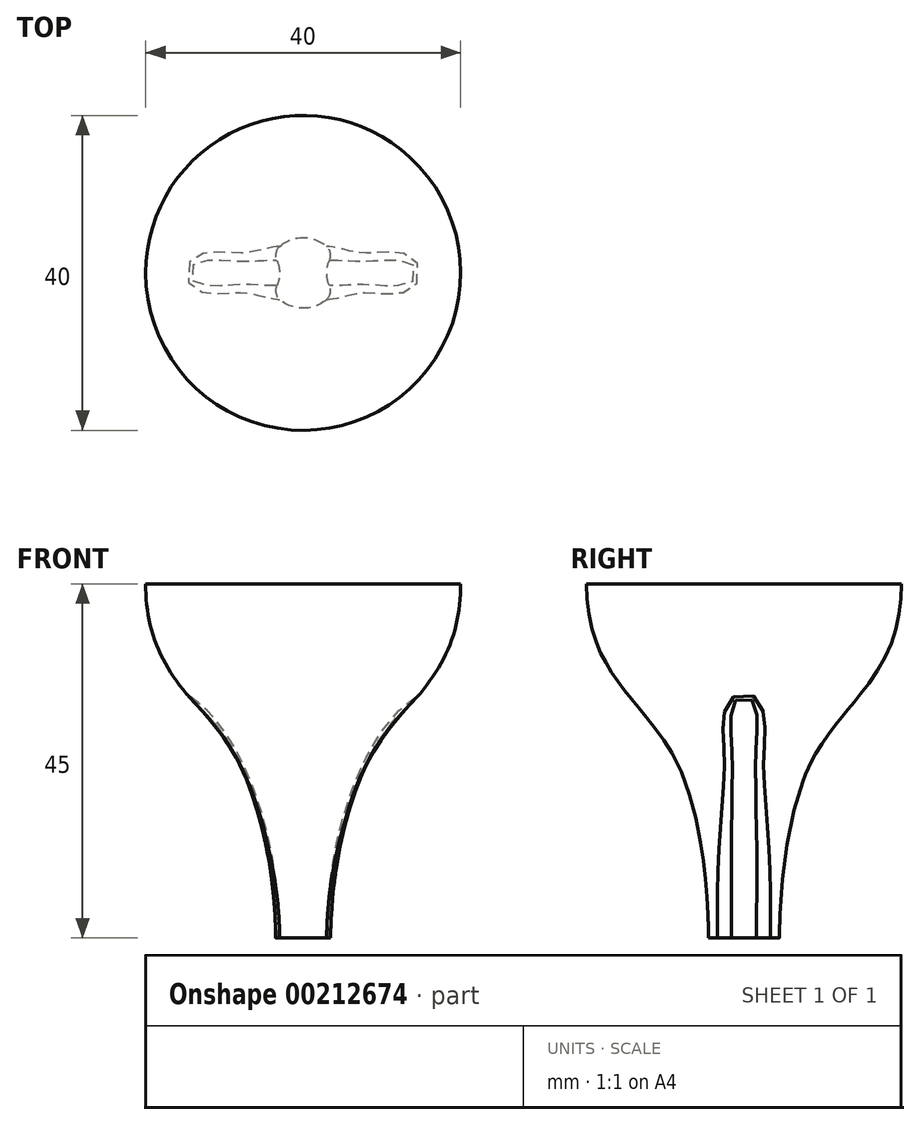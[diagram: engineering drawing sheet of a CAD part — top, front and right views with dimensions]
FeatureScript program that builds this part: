
annotation { "Feature Type Name" : "Feature", "Feature Type Description" : "" }
export const myFeature = defineFeature(function(context is Context, id is Id, definition is map)
    precondition{}
    {
        {
            var Q0;
            Q0=qCreatedBy(makeId("Front.planeOp"),FACE);
            var sketch = newSketch(context, id + "F0", { "sketchPlane" : qUnion([Q0])});
            skLineSegment(sketch, "E0", {"start": v(0, 0) * mm, "end": v(6, 0) * mm, "construction": true});
            skLineSegment(sketch, "E1", {"start": v(0, 0) * mm, "end": v(0, -15) * mm});
            skLineSegment(sketch, "E2", {"start": v(0, 0) * mm, "end": v(0, 30) * mm});
            skLineSegment(sketch, "E3", {"start": v(0, 30) * mm, "end": v(20, 30) * mm});
            skLineSegment(sketch, "E4", {"start": v(0, -15) * mm, "end": v(4.5, -15) * mm});
            skFitSpline(sketch, "E5", {"points": [v(20, 30) * mm, v(8.26, 6.8) * mm, v(4.5, -15) * mm], "startDerivative": vector(0, -69.69) * mm, "endDerivative": vector(0, -11.28) * mm});
            skFitSpline(sketch, "E6", {"points": [v(4.5, -15) * mm, v(19.07, 15.63) * mm], "startDerivative": vector(0, 47.54) * mm, "endDerivative": vector(23.28, 0) * mm});
            skFitSpline(sketch, "E7.MirrorCS", {"points": [v(-4.5, -15) * mm, v(-19.07, 15.63) * mm], "startDerivative": vector(0, 47.54) * mm, "endDerivative": vector(-23.28, 0) * mm});
            skSolve(sketch);
        }
        {
            var Q0;
            Q0 = qSketchRegion(id + "F0", true);
            var Q1;
            Q1=sQuery(id+"F0.wireOp",EDGE,"E2");
            revolve(context, id + "F1", {"entities" : qUnion([Q0]), "axis" : qUnion([Q1]), "revolveType" : RevolveType.FULL});
        }
        {
            var Q0;
            Q0=makeQuery(id+"F1.opRevolve","SWEPT_FACE",FACE,{"disambiguationData":[OSD([sQuery(id+"F0.wireOp",EDGE,"E4")])]});
            var sketch = newSketch(context, id + "F2", { "sketchPlane" : qUnion([Q0])});
            skEllipse(sketch, "E8", {"center": v(4.5, 0) * mm, "majorRadius": 1.5 * mm, "minorRadius": 2.5 * mm, "majorAxis": v(1, 0)});
            skLineSegment(sketch, "E9", {"start": v(0, 0) * mm, "end": v(0, 4.5) * mm, "construction": true});
            skEllipse(sketch, "E10.MirrorC", {"center": v(-4.5, 0) * mm, "majorRadius": 1.5 * mm, "minorRadius": 2.5 * mm, "majorAxis": v(-1, 0)});
            skSolve(sketch);
        }
        {
            var Q0;
            {var subQ0=sQuery(id+"F2.wireOp",EDGE,"E8");var subQ1=makeQuery(id+"F1.opRevolve","SWEPT_EDGE",EDGE,{"disambiguationData":[OSD([sQuery(id+"F0.wireOp",EDGE,"E4"),sQuery(id+"F0.wireOp",EDGE,"E5"),sQuery(id+"F0.wireOp",EDGE,"E6")])]});var subQ2=makeQuery(id+"F2.imprint","INTERSECT",VERTEX,{"disambiguationData":[OD(0.0)],"derivedFrom":[subQ1,subQ0]});Q0=makeQuery(id+"F2.imprint","IMPRINT",FACE,{"disambiguationData":[TD([[makeQuery(id+"F2.imprint","IMPRINT",EDGE,{"disambiguationData":[TD([[subQ2,-1.0]])],"derivedFrom":subQ0}),1.0]])]});}
            var Q1;
            {var subQ0=sQuery(id+"F2.wireOp",EDGE,"E8");var subQ1=makeQuery(id+"F1.opRevolve","SWEPT_EDGE",EDGE,{"disambiguationData":[OSD([sQuery(id+"F0.wireOp",EDGE,"E4"),sQuery(id+"F0.wireOp",EDGE,"E5"),sQuery(id+"F0.wireOp",EDGE,"E6")])]});var subQ2=makeQuery(id+"F2.imprint","INTERSECT",VERTEX,{"disambiguationData":[OD(0.0)],"derivedFrom":[subQ1,subQ0]});Q1=makeQuery(id+"F2.imprint","IMPRINT",FACE,{"disambiguationData":[TD([[makeQuery(id+"F2.imprint","IMPRINT",EDGE,{"disambiguationData":[TD([[subQ2,1.0]])],"derivedFrom":subQ0}),1.0]])]});}
            var Q2;
            Q2=sQuery(id+"F0.wireOp",EDGE,"E6");
            sweep(context, id + "F3", {"operationType" : NewBodyOperationType.REMOVE, "profiles" : qUnion([Q0, Q1]), "path" : qUnion([Q2])});
        }
        {
            var Q0;
            {var subQ0=sQuery(id+"F2.wireOp",EDGE,"E10.MirrorC");var subQ1=makeQuery(id+"F1.opRevolve","SWEPT_EDGE",EDGE,{"disambiguationData":[OSD([sQuery(id+"F0.wireOp",EDGE,"E4"),sQuery(id+"F0.wireOp",EDGE,"E5"),sQuery(id+"F0.wireOp",EDGE,"E6")])]});var subQ2=makeQuery(id+"F2.imprint","INTERSECT",VERTEX,{"disambiguationData":[OD(0.0)],"derivedFrom":[subQ1,subQ0]});Q0=makeQuery(id+"F2.imprint","IMPRINT",FACE,{"disambiguationData":[TD([[makeQuery(id+"F2.imprint","IMPRINT",EDGE,{"disambiguationData":[TD([[subQ2,-1.0]])],"derivedFrom":subQ0}),1.0]])]});}
            var Q1;
            {var subQ0=sQuery(id+"F2.wireOp",EDGE,"E10.MirrorC");var subQ1=makeQuery(id+"F1.opRevolve","SWEPT_EDGE",EDGE,{"disambiguationData":[OSD([sQuery(id+"F0.wireOp",EDGE,"E4"),sQuery(id+"F0.wireOp",EDGE,"E5"),sQuery(id+"F0.wireOp",EDGE,"E6")])]});var subQ2=makeQuery(id+"F2.imprint","INTERSECT",VERTEX,{"disambiguationData":[OD(0.0)],"derivedFrom":[subQ1,subQ0]});Q1=makeQuery(id+"F2.imprint","IMPRINT",FACE,{"disambiguationData":[TD([[makeQuery(id+"F2.imprint","IMPRINT",EDGE,{"disambiguationData":[TD([[subQ2,1.0]])],"derivedFrom":subQ0}),1.0]])]});}
            var Q2;
            Q2=sQuery(id+"F0.wireOp",EDGE,"E7.MirrorCS");
            sweep(context, id + "F4", {"operationType" : NewBodyOperationType.REMOVE, "profiles" : qUnion([Q0, Q1]), "path" : qUnion([Q2])});
        }
        {
            var Q0;
            Q0=makeQuery(id+"F4.boolean.opBoolean","INTERSECT",EDGE,{"derivedFrom":[makeQuery(id+"F1.opRevolve","SWEPT_FACE",FACE,{"disambiguationData":[OSD([sQuery(id+"F0.wireOp",EDGE,"E5")])]}),makeQuery(id+"F4.opSweep","SWEPT_FACE",FACE,{"disambiguationData":[OSD([sQuery(id+"F0.wireOp",EDGE,"E7.MirrorCS"),sQuery(id+"F2.wireOp",EDGE,"E10.MirrorC")])]})]});
            var Q1;
            Q1=makeQuery(id+"F3.boolean.opBoolean","INTERSECT",EDGE,{"derivedFrom":[makeQuery(id+"F1.opRevolve","SWEPT_FACE",FACE,{"disambiguationData":[OSD([sQuery(id+"F0.wireOp",EDGE,"E5")])]}),makeQuery(id+"F3.opSweep","SWEPT_FACE",FACE,{"disambiguationData":[OSD([sQuery(id+"F0.wireOp",EDGE,"E6"),sQuery(id+"F2.wireOp",EDGE,"E8")])]})]});
            fillet(context, id + "F5", {"entities" : qUnion([Q0, Q1]), "radius" : 1.5 * mm, "tangentPropagation" : true, "allowEdgeOverflow" : false});
        }
    });
